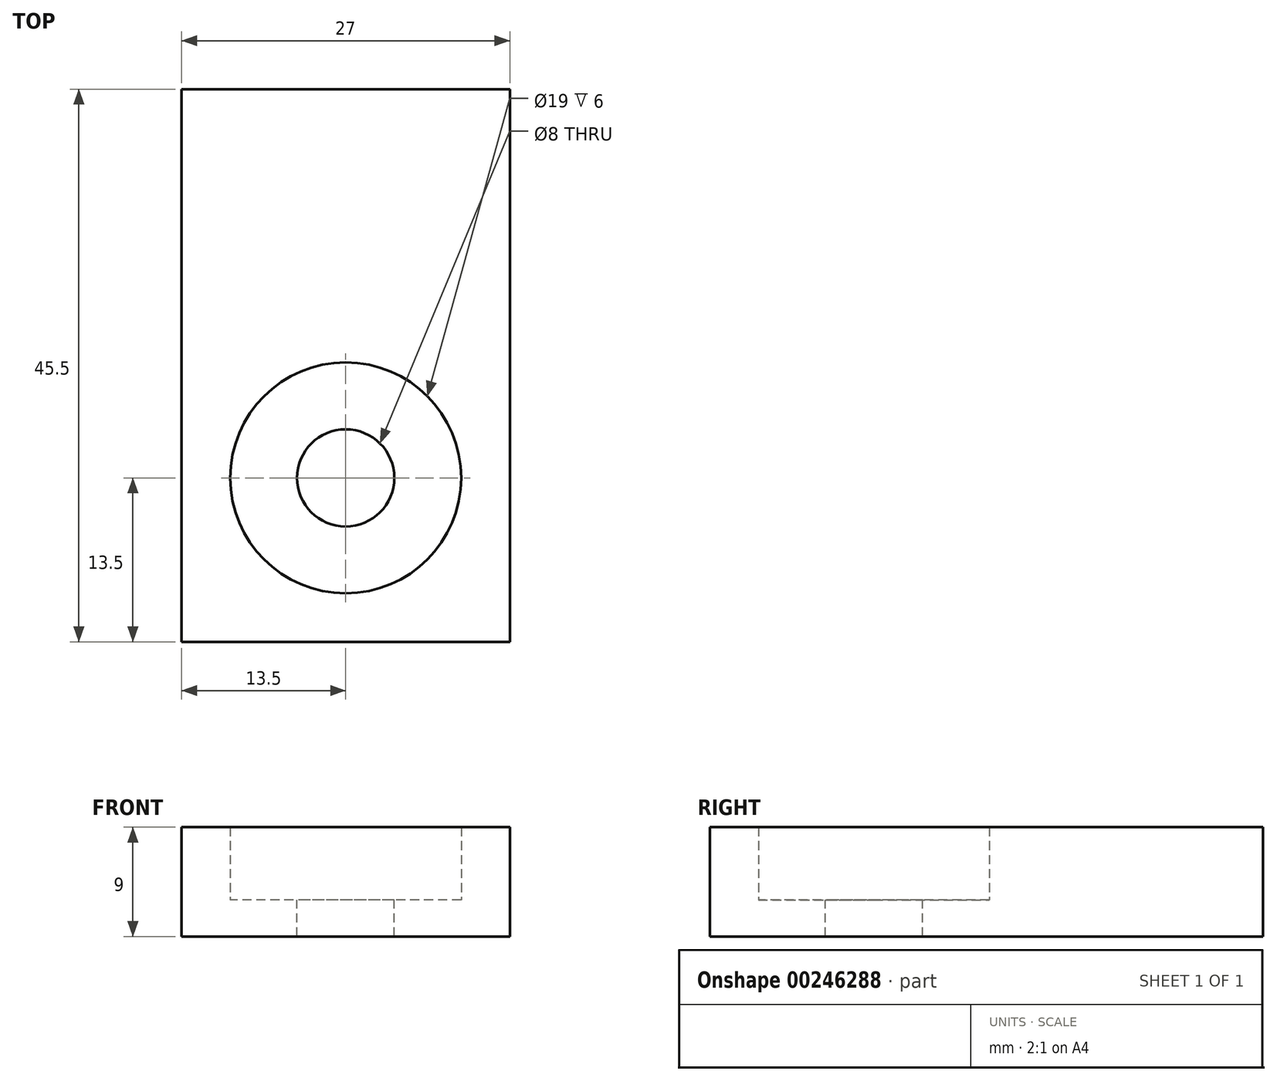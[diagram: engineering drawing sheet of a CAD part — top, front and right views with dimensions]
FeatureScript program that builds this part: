
annotation { "Feature Type Name" : "Feature", "Feature Type Description" : "" }
export const myFeature = defineFeature(function(context is Context, id is Id, definition is map)
    precondition{}
    {
        {
            var Q0;
            Q0=qCreatedBy(makeId("Top.planeOp"),FACE);
            var sketch = newSketch(context, id + "F0", { "sketchPlane" : qUnion([Q0])});
            skLineSegment(sketch, "E0.bottom", {"start": v(-13.5, 13.5) * mm, "end": v(13.5, 13.5) * mm, "construction": true});
            skLineSegment(sketch, "E0.top", {"start": v(-13.5, -13.5) * mm, "end": v(13.5, -13.5) * mm});
            skLineSegment(sketch, "E0.left", {"start": v(-13.5, 32) * mm, "end": v(-13.5, -13.5) * mm});
            skLineSegment(sketch, "E0.right", {"start": v(13.5, 32) * mm, "end": v(13.5, -13.5) * mm});
            skPoint(sketch, "E1", {"position": v(0, 13.5) * mm});
            skPoint(sketch, "E2", {"position": v(-13.5, 0) * mm});
            skCircle(sketch, "E3", {"center": v(0, 0) * mm, "radius": 9.5 * mm});
            skCircle(sketch, "E4", {"center": v(0, 0) * mm, "radius": 4 * mm});
            skLineSegment(sketch, "E5", {"start": v(-13.5, 32) * mm, "end": v(13.5, 32) * mm});
            skSolve(sketch);
        }
        {
            var Q0;
            Q0 = qSketchRegion(id + "F0", true);
            extrude(context, id + "F1", {"entities" : qUnion([Q0]), "depth" : 6 * mm});
        }
        {
            var Q0;
            Q0=makeQuery(id+"F0.imprint","IMPRINT",FACE,{"disambiguationData":[TD([[makeQuery(id+"F0.imprint","IMPRINT",EDGE,{"derivedFrom":sQuery(id+"F0.wireOp",EDGE,"E0.bottom")}),-1.0]])]});
            var Q1;
            Q1=makeQuery(id+"F0.imprint","IMPRINT",FACE,{"disambiguationData":[TD([[makeQuery(id+"F0.imprint","IMPRINT",EDGE,{"derivedFrom":sQuery(id+"F0.wireOp",EDGE,"E3")}),1.0]])]});
            var Q2;
            Q2=makeQuery(id+"F0.imprint","IMPRINT",FACE,{"disambiguationData":[TD([[makeQuery(id+"F0.imprint","IMPRINT",EDGE,{"derivedFrom":sQuery(id+"F0.wireOp",EDGE,"E0.top")}),1.0]])]});
            extrude(context, id + "F2", {"entities" : qUnion([Q0, Q1, Q2]), "operationType" : NewBodyOperationType.ADD, "oppositeDirection" : true, "depth" : 3 * mm});
        }
    });
